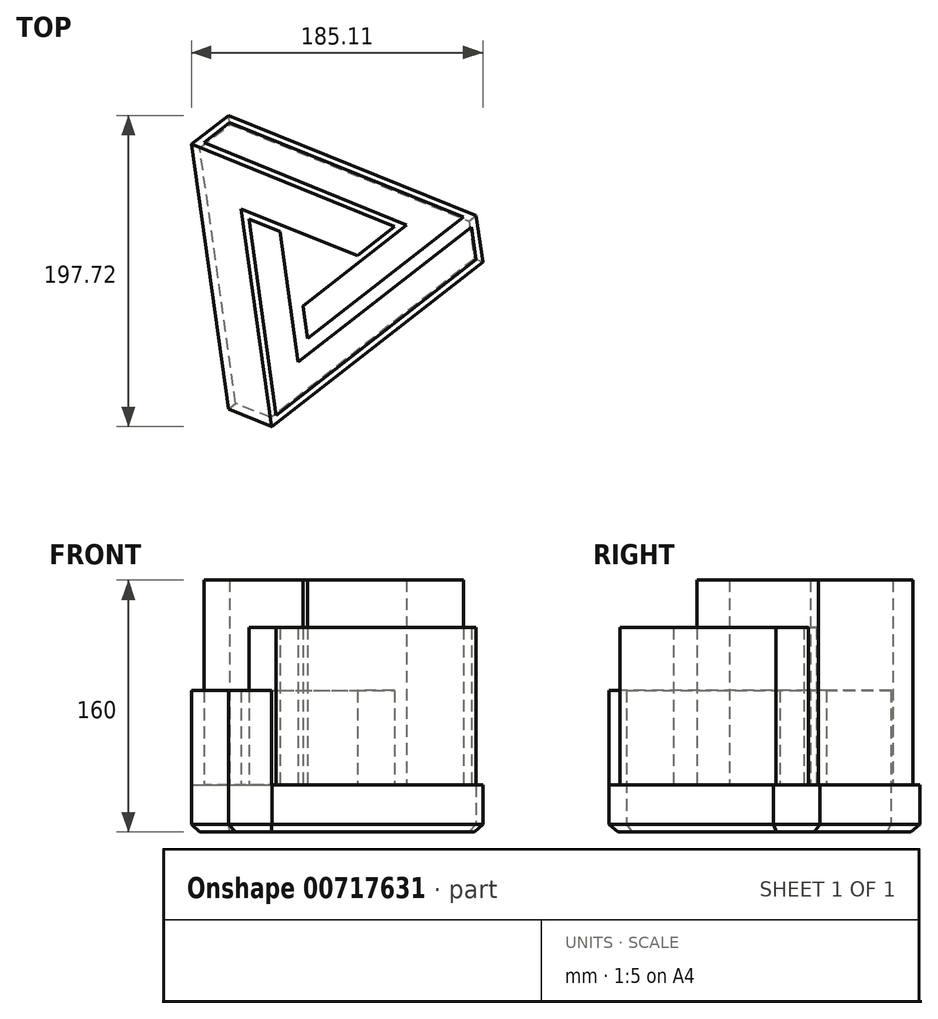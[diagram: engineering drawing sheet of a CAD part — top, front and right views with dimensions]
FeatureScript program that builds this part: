
annotation { "Feature Type Name" : "Feature", "Feature Type Description" : "" }
export const myFeature = defineFeature(function(context is Context, id is Id, definition is map)
    precondition{}
    {
        {
            var Q0;
            Q0=qCreatedBy(makeId("Top.planeOp"),FACE);
            var sketch = newSketch(context, id + "F0", { "sketchPlane" : qUnion([Q0])});
            skLineSegment(sketch, "E0.0", {"start": v(94.23, 28.58) * mm, "end": v(-39.49, -75.85) * mm});
            skLineSegment(sketch, "E0.1", {"start": v(-67.3, -64.6) * mm, "end": v(-90.88, 103.4) * mm});
            skLineSegment(sketch, "E0.2", {"start": v(-67.23, 121.87) * mm, "end": v(90.06, 58.28) * mm});
            skPoint(sketch, "E0.0.midPoint", {"position": v(27.37, -23.64) * mm});
            skLineSegment(sketch, "E1", {"start": v(-90.88, 103.4) * mm, "end": v(-67.23, 121.87) * mm});
            skLineSegment(sketch, "E2", {"start": v(90.06, 58.28) * mm, "end": v(94.23, 28.58) * mm});
            skLineSegment(sketch, "E3", {"start": v(-67.3, -64.6) * mm, "end": v(-39.49, -75.85) * mm});
            skPoint(sketch, "E4.orphan", {"position": v(-95.05, 133.12) * mm});
            skPoint(sketch, "E5.orphan", {"position": v(117.87, 47.04) * mm});
            skPoint(sketch, "E6.orphan", {"position": v(-63.13, -94.31) * mm});
            skSolve(sketch);
        }
        {
            var Q0;
            Q0 = qSketchRegion(id + "F0", true);
            extrude(context, id + "F1", {"entities" : qUnion([Q0]), "depth" : 30 * mm, "offsetDistance" : 25 * mm});
        }
        {
            var Q0;
            Q0=makeQuery(id+"F1.opExtrude","CAP_FACE",FACE,{"disambiguationData":[OSD([sQuery(id+"F0.wireOp",EDGE,"E0.0"),sQuery(id+"F0.wireOp",EDGE,"E0.1"),sQuery(id+"F0.wireOp",EDGE,"E0.2"),sQuery(id+"F0.wireOp",EDGE,"E1"),sQuery(id+"F0.wireOp",EDGE,"E2"),sQuery(id+"F0.wireOp",EDGE,"E3")])],"isStart":false});
            var sketch = newSketch(context, id + "F2", { "sketchPlane" : qUnion([Q0])});
            skLineSegment(sketch, "E7", {"start": v(38, 51.15) * mm, "end": v(-24.14, 2.46) * mm});
            skLineSegment(sketch, "E8", {"start": v(-59.29, 62.46) * mm, "end": v(14.6, 32.81) * mm});
            skLineSegment(sketch, "E9", {"start": v(-91.1, 103.7) * mm, "end": v(38, 51.15) * mm});
            skLineSegment(sketch, "E10", {"start": v(90.3, 58.7) * mm, "end": v(-20, -27.28) * mm});
            skLineSegment(sketch, "E11.trimOffspring", {"start": v(-59.29, 62.46) * mm, "end": v(-39.8, -77.45) * mm});
            skLineSegment(sketch, "E12.trimOffspring", {"start": v(-30.9, 51.07) * mm, "end": v(-20, -27.28) * mm});
            skSolve(sketch);
        }
        {
            var Q0;
            {var subQ0=sQuery(id+"F2.wireOp",EDGE,"E9");var subQ1=sQuery(id+"F2.wireOp",EDGE,"E7");var subQ2=makeQuery(id+"F2.imprint","INTERSECT",VERTEX,{"derivedFrom":[subQ1,subQ0]});Q0=makeQuery(id+"F2.imprint","IMPRINT",FACE,{"disambiguationData":[TD([[makeQuery(id+"F2.imprint","IMPRINT",EDGE,{"disambiguationData":[TD([[subQ2,-1.0]])],"derivedFrom":subQ1}),1.0]])]});}
            var sketch = newSketch(context, id + "F3", { "sketchPlane" : qUnion([Q0])});
            skLineSegment(sketch, "E13.0", {"start": v(-19.86, 0.73) * mm, "end": v(-17, -19.86) * mm});
            skLineSegment(sketch, "E13.1", {"start": v(17.07, 29.67) * mm, "end": v(-19.86, 0.73) * mm});
            skLineSegment(sketch, "E13.2", {"start": v(81.94, 57.25) * mm, "end": v(-66.6, 117.3) * mm});
            skLineSegment(sketch, "E13.3", {"start": v(-66.6, 117.3) * mm, "end": v(-82.8, 104.64) * mm});
            skLineSegment(sketch, "E13.4", {"start": v(-82.8, 104.64) * mm, "end": v(45.9, 52.25) * mm});
            skLineSegment(sketch, "E13.5", {"start": v(-17, -19.86) * mm, "end": v(81.94, 57.25) * mm});
            skLineSegment(sketch, "E13.6", {"start": v(45.9, 52.25) * mm, "end": v(17.07, 29.67) * mm});
            skSolve(sketch);
        }
        {
            var Q0;
            {var subQ10=makeQuery(id+"F1.opExtrude","CAP_EDGE",EDGE,{"disambiguationData":[OSD([sQuery(id+"F0.wireOp",EDGE,"E0.0")])],"isStart":false});Q0=makeQuery(id+"F2.imprint","IMPRINT",FACE,{"disambiguationData":[TD([[makeQuery(id+"F2.imprint","IMPRINT",EDGE,{"derivedFrom":subQ10}),-1.0]])]});}
            var sketch = newSketch(context, id + "F4", { "sketchPlane" : qUnion([Q0])});
            skLineSegment(sketch, "E14.0", {"start": v(-23, -34.7) * mm, "end": v(-28.1, 1.9) * mm});
            skLineSegment(sketch, "E14.1", {"start": v(87.03, 51.08) * mm, "end": v(-23, -34.7) * mm});
            skLineSegment(sketch, "E14.2", {"start": v(-34.55, 48.22) * mm, "end": v(-54.38, 56.18) * mm});
            skLineSegment(sketch, "E14.3", {"start": v(-54.38, 56.18) * mm, "end": v(-36.97, -68.81) * mm});
            skLineSegment(sketch, "E14.4", {"start": v(-36.97, -68.81) * mm, "end": v(89.95, 30.3) * mm});
            skLineSegment(sketch, "E14.5", {"start": v(-28.1, 1.9) * mm, "end": v(-34.55, 48.22) * mm});
            skLineSegment(sketch, "E14.6", {"start": v(89.95, 30.3) * mm, "end": v(87.03, 51.08) * mm});
            skSolve(sketch);
        }
        {
            var Q0;
            {var subQ8=makeQuery(id+"F1.opExtrude","CAP_EDGE",EDGE,{"disambiguationData":[OSD([sQuery(id+"F0.wireOp",EDGE,"E0.1")])],"isStart":false});Q0=makeQuery(id+"F2.imprint","IMPRINT",FACE,{"disambiguationData":[TD([[makeQuery(id+"F2.imprint","IMPRINT",EDGE,{"derivedFrom":subQ8}),-1.0]])]});}
            extrude(context, id + "F5", {"entities" : qUnion([Q0]), "operationType" : NewBodyOperationType.ADD, "depth" : 60 * mm, "offsetDistance" : 25 * mm});
        }
        {
            var Q0;
            Q0=makeQuery(id+"F4.imprint","IMPRINT",FACE,{"disambiguationData":[TD([[makeQuery(id+"F4.imprint","IMPRINT",EDGE,{"derivedFrom":sQuery(id+"F4.wireOp",EDGE,"E14.0")}),1.0]])]});
            extrude(context, id + "F6", {"entities" : qUnion([Q0]), "operationType" : NewBodyOperationType.ADD, "depth" : 100 * mm, "offsetDistance" : 25 * mm});
        }
        {
            var Q0;
            Q0=makeQuery(id+"F3.imprint","IMPRINT",FACE,{"disambiguationData":[TD([[makeQuery(id+"F3.imprint","IMPRINT",EDGE,{"derivedFrom":sQuery(id+"F3.wireOp",EDGE,"E13.0")}),1.0]])]});
            extrude(context, id + "F7", {"entities" : qUnion([Q0]), "operationType" : NewBodyOperationType.ADD, "depth" : 130 * mm, "offsetDistance" : 25 * mm});
        }
        {
            var Q0;
            Q0=makeQuery(id+"F1.opExtrude","CAP_EDGE",EDGE,{"disambiguationData":[OSD([sQuery(id+"F0.wireOp",EDGE,"E0.2")])],"isStart":true});
            var Q1;
            Q1=makeQuery(id+"F1.opExtrude","CAP_EDGE",EDGE,{"disambiguationData":[OSD([sQuery(id+"F0.wireOp",EDGE,"E2")])],"isStart":true});
            var Q2;
            Q2=makeQuery(id+"F1.opExtrude","CAP_EDGE",EDGE,{"disambiguationData":[OSD([sQuery(id+"F0.wireOp",EDGE,"E0.0")])],"isStart":true});
            var Q3;
            Q3=makeQuery(id+"F1.opExtrude","CAP_EDGE",EDGE,{"disambiguationData":[OSD([sQuery(id+"F0.wireOp",EDGE,"E1")])],"isStart":true});
            var Q4;
            Q4=makeQuery(id+"F1.opExtrude","CAP_EDGE",EDGE,{"disambiguationData":[OSD([sQuery(id+"F0.wireOp",EDGE,"E0.1")])],"isStart":true});
            var Q5;
            Q5=makeQuery(id+"F1.opExtrude","CAP_EDGE",EDGE,{"disambiguationData":[OSD([sQuery(id+"F0.wireOp",EDGE,"E3")])],"isStart":true});
            chamfer(context, id + "F8", {"entities" : qUnion([Q0, Q1, Q2, Q3, Q4, Q5]), "width" : 5 * mm, "tangentPropagation" : true});
        }
    });
